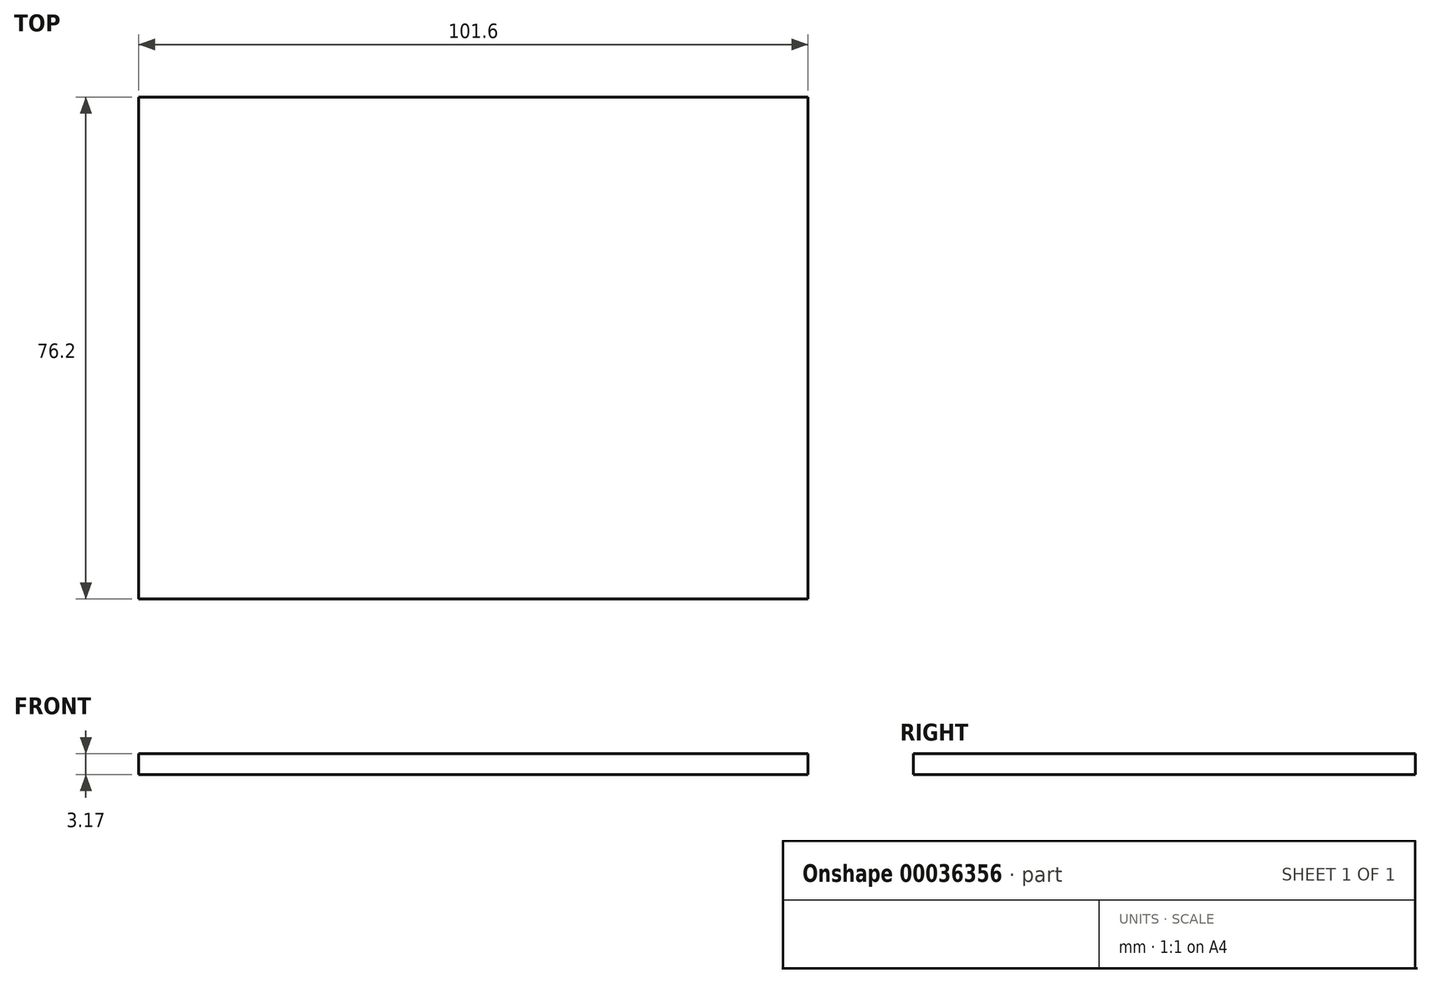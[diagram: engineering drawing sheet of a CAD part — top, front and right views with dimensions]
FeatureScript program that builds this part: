
annotation { "Feature Type Name" : "Feature", "Feature Type Description" : "" }
export const myFeature = defineFeature(function(context is Context, id is Id, definition is map)
    precondition{}
    {
        {
            var Q0;
            Q0=qCreatedBy(makeId("Top.planeOp"),FACE);
            var sketch = newSketch(context, id + "F0", { "sketchPlane" : qUnion([Q0])});
            skLineSegment(sketch, "E0.rect.bottom", {"start": v(-50.8, 38.1) * mm, "end": v(50.8, 38.1) * mm});
            skLineSegment(sketch, "E0.rect.top", {"start": v(-50.8, -38.1) * mm, "end": v(50.8, -38.1) * mm});
            skLineSegment(sketch, "E0.rect.left", {"start": v(-50.8, 38.1) * mm, "end": v(-50.8, -38.1) * mm});
            skLineSegment(sketch, "E0.rect.right", {"start": v(50.8, 38.1) * mm, "end": v(50.8, -38.1) * mm});
            skPoint(sketch, "E0.rect.middle", {"position": v(0, 0) * mm});
            skSolve(sketch);
        }
        {
            var Q0;
            Q0=makeQuery(id+"F0.imprint","IMPRINT",FACE,{"disambiguationData":[TD([[makeQuery(id+"F0.imprint","IMPRINT",EDGE,{"derivedFrom":sQuery(id+"F0.wireOp",EDGE,"E0.rect.bottom")}),-1.0]])]});
            extrude(context, id + "F1", {"entities" : qUnion([Q0]), "depth" : 3.17 * mm});
        }
    });
